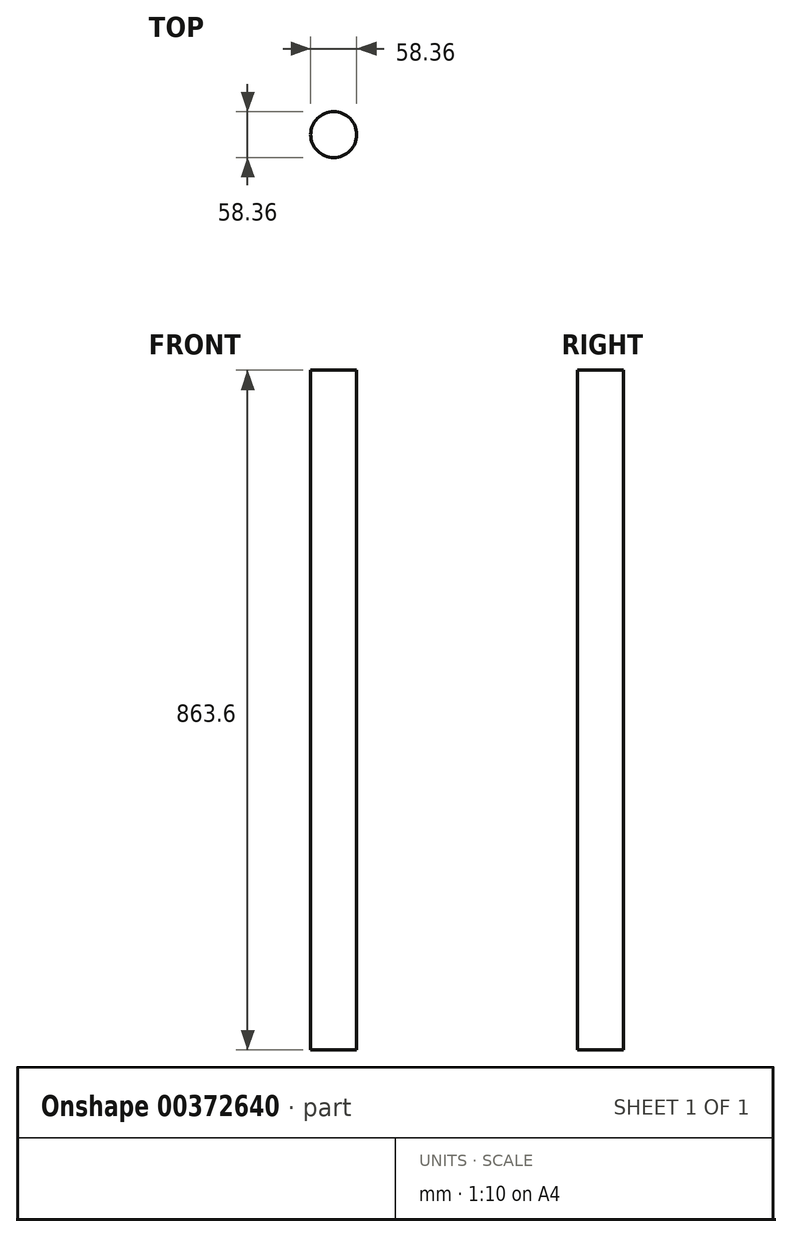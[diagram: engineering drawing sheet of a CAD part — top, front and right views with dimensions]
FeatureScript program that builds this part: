
annotation { "Feature Type Name" : "Feature", "Feature Type Description" : "" }
export const myFeature = defineFeature(function(context is Context, id is Id, definition is map)
    precondition{}
    {
        {
            var Q0;
            Q0=qCreatedBy(makeId("Top.planeOp"),FACE);
            var sketch = newSketch(context, id + "F0", { "sketchPlane" : qUnion([Q0])});
            skCircle(sketch, "E0", {"center": v(0, 0) * mm, "radius": 29.18 * mm});
            skSolve(sketch);
        }
        {
            var Q0;
            Q0=sQuery(id+"F0.wireOp",EDGE,"E0");
            extrude(context, id + "F1", {"bodyType" : ToolBodyType.SURFACE, "surfaceEntities" : qUnion([Q0]), "depth" : 25.4 * mm});
        }
        {
            var Q0;
            Q0 = qSketchRegion(id + "F0", true);
            extrude(context, id + "F2", {"entities" : qUnion([Q0]), "oppositeDirection" : true, "depth" : 863.6 * mm});
        }
    });
